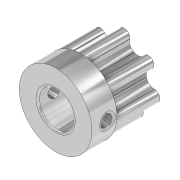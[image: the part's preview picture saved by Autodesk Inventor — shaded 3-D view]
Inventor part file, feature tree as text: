
AUTODESK INVENTOR PART (.ipt)
format: ipt  version: 2020 (Build 240168000, 168)  size: 380,928 bytes
history: native  units: in
note: dims shown in document units (in); Inventor stores cm internally (conversion verified against a paired STEP export)
features: chamfer x8, extrude x3, sketch x3, fillet x1
ambient origin geometry x8: Origin, YZ Plane, XZ Plane, XY Plane, X Axis, Y Axis, Z Axis, Center Point
bodies: Solid1 (feature_tree)
feature tree (15):
  extrude  "Extrusion1"  Depth=0.4724in
  extrude  "Extrusion2"  Depth=0.084in
  extrude  "Extrusion3"  Depth=0.084in
  chamfer  "Chamfer1"  Distance=2.7559in Angle=360.0deg
  fillet  "Fillet1"  Radius=0.2362in
  chamfer  "Chamfer3"  Distance=0.1969in
  chamfer  "Chamfer4"  Distance=0.0748in
  chamfer  "Chamfer5"  Distance=0.1575in
  chamfer  "Chamfer6"  Distance=0.2756in
  chamfer  "Chamfer7"  Distance=0.0118in
  chamfer  "Chamfer8"  Distance=0.0079in
  chamfer  "Chamfer9"  Distance=0.0394in Angle=45.0deg
  sketch  "Sketch1"  dims[d0=0.2047in d1=0.4724in]
  sketch  "Sketch2"  dims[d2=0.0866in d5=0.084in]
  sketch  "Sketch3"  dims[d6=0.084in d7=0.084in d8=2.7559in d10=360.0deg d12=0.2362in d13=0.0in d14=0.1969in d15=0.0in d16=0.0748in d17=0.1575in d18=0.0in d19=0.2756in d20=0.125in d21=0.0137in d22=0.0118in d23=0.0079in d28=0.0394in d29=0.0866in d30=45.0deg d31=0.0394in d32=0.0866in d33=45.0deg d34=0.0394in d35=0.0866in d36=45.0deg d37=0.0394in d38=0.0866in d39=45.0deg d40=0.0394in d41=0.0866in d42=45.0deg d43=0.0394in d44=0.0866in d45=45.0deg d46=0.0394in d47=0.0866in d48=45.0deg d24=0.5in d25=0.0344in d26=0.5in d27=0.0344in]
